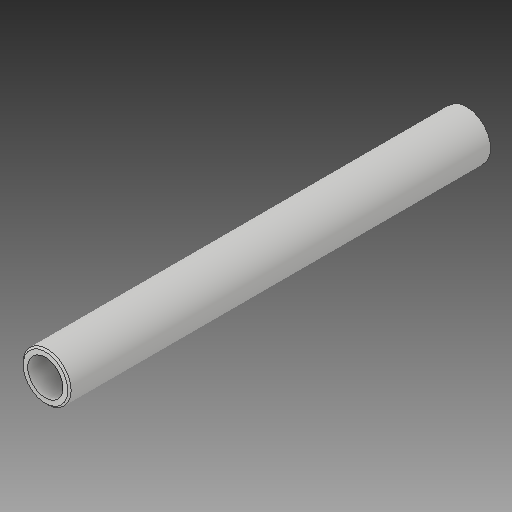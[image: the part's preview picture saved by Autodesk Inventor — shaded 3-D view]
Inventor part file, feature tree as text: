
AUTODESK INVENTOR PART (.ipt)
format: ipt  version: 2018 (Build 220112000, 112)  size: 95,744 bytes
history: native  units: mm
features: extrude x1, chamfer x1, sketch x1
ambient origin geometry x8: Origin, YZ Plane, XZ Plane, XY Plane, X Axis, Y Axis, Z Axis, Center Point
bodies: Solid1 (feature_tree)
feature tree (3):
  extrude  "Extrusion1"  Depth=500.72mm
  chamfer  "Chamfer1"  Distance=500.72mm
  sketch  "Sketch1"  dims[d0=57.2mm d1=41.9mm d2=500.72mm d3=0.0mm d4=2.0mm d5=2.0mm d6=45.0deg]
